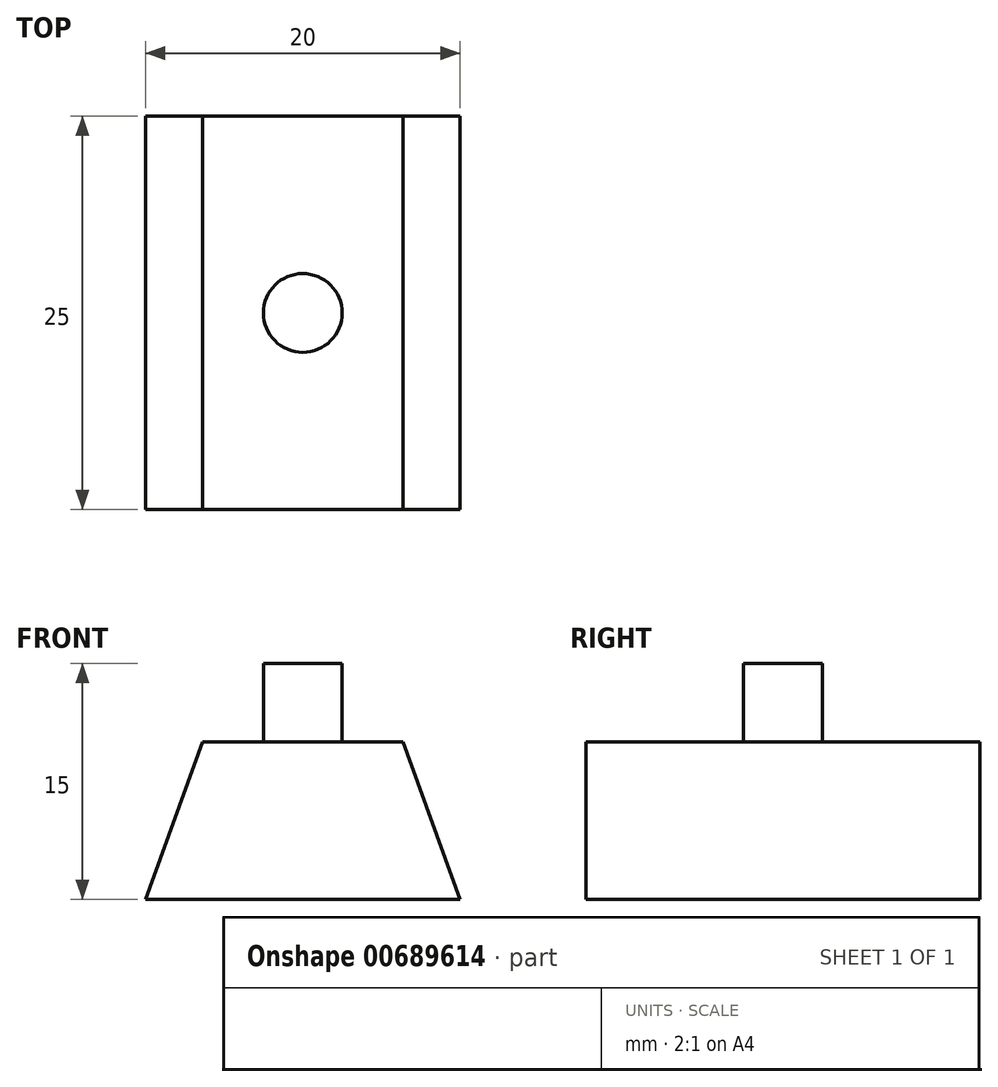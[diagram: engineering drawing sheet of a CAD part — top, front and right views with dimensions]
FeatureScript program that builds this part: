
annotation { "Feature Type Name" : "Feature", "Feature Type Description" : "" }
export const myFeature = defineFeature(function(context is Context, id is Id, definition is map)
    precondition{}
    {
        {
            var Q0;
            Q0=qCreatedBy(makeId("Front.planeOp"),FACE);
            var sketch = newSketch(context, id + "F0", { "sketchPlane" : qUnion([Q0])});
            skLineSegment(sketch, "E0", {"start": v(0, 0) * mm, "end": v(20, 0) * mm});
            skLineSegment(sketch, "E1", {"start": v(10, 10) * mm, "end": v(3.64, 10) * mm});
            skLineSegment(sketch, "E2", {"start": v(10, 10) * mm, "end": v(16.36, 10) * mm});
            skLineSegment(sketch, "E3", {"start": v(16.36, 10) * mm, "end": v(20, 0) * mm});
            skLineSegment(sketch, "E4", {"start": v(3.64, 10) * mm, "end": v(0, 0) * mm});
            skSolve(sketch);
        }
        {
            var Q0;
            Q0=makeQuery(id+"F0.imprint","IMPRINT",FACE,{"disambiguationData":[TD([[makeQuery(id+"F0.imprint","IMPRINT",EDGE,{"derivedFrom":sQuery(id+"F0.wireOp",EDGE,"E0")}),1.0]])]});
            extrude(context, id + "F1", {"entities" : qUnion([Q0]), "depth" : 25 * mm, "offsetDistance" : 25 * mm});
        }
        {
            var Q0;
            Q0=qCreatedBy(makeId("Top.planeOp"),FACE);
            var sketch = newSketch(context, id + "F2", { "sketchPlane" : qUnion([Q0])});
            skCircle(sketch, "E5", {"center": v(10, -12.5) * mm, "radius": 2.5 * mm});
            skSolve(sketch);
        }
        {
            var Q0;
            Q0=makeQuery(id+"F2.imprint","IMPRINT",FACE,{"disambiguationData":[TD([[makeQuery(id+"F2.imprint","IMPRINT",EDGE,{"derivedFrom":sQuery(id+"F2.wireOp",EDGE,"E5")}),1.0]])]});
            extrude(context, id + "F3", {"entities" : qUnion([Q0]), "operationType" : NewBodyOperationType.ADD, "depth" : 15 * mm, "offsetDistance" : 25 * mm});
        }
    });
